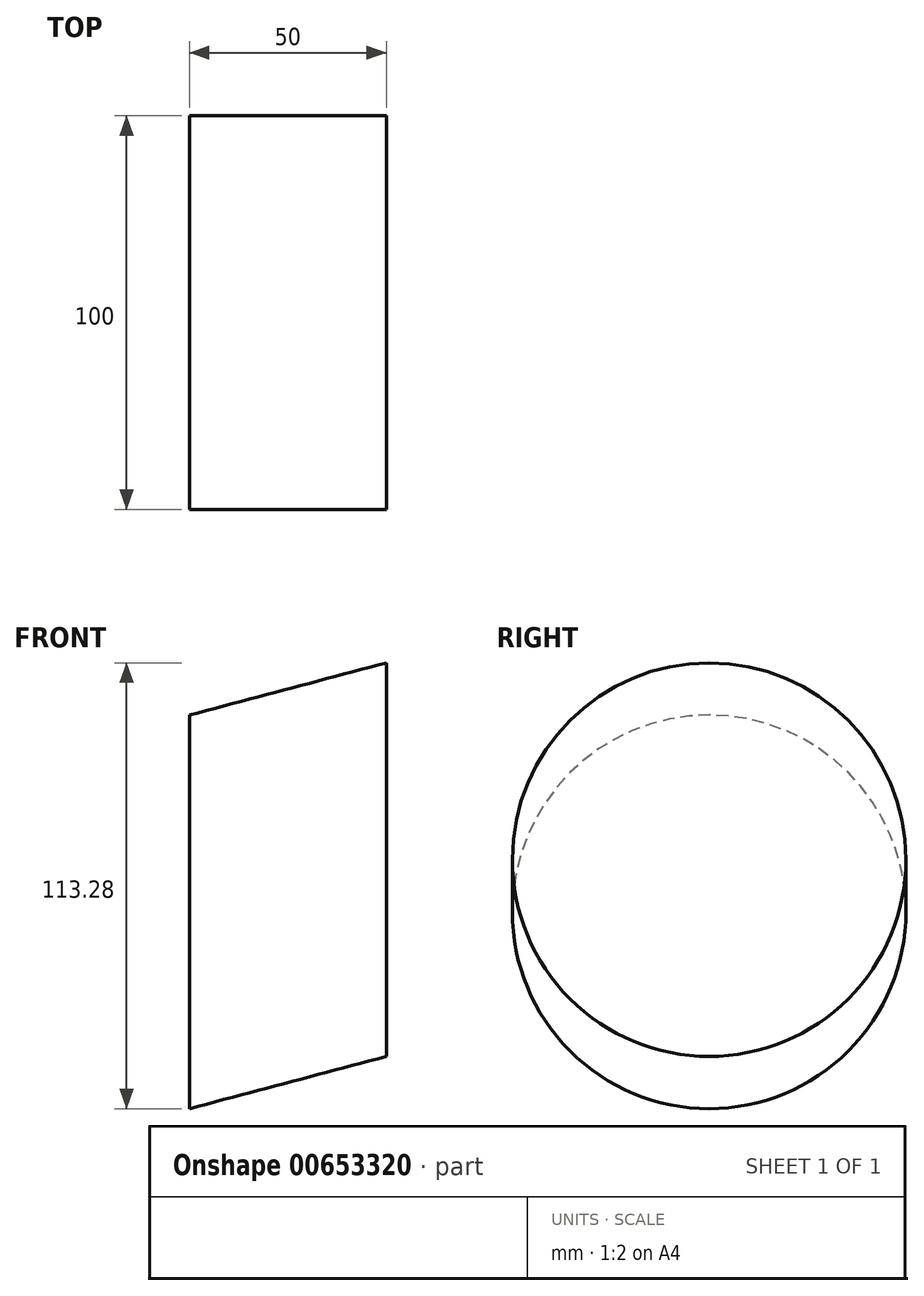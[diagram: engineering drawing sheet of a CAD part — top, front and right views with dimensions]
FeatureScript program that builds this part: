
annotation { "Feature Type Name" : "Feature", "Feature Type Description" : "" }
export const myFeature = defineFeature(function(context is Context, id is Id, definition is map)
    precondition{}
    {
        {
            var Q0;
            Q0=qCreatedBy(makeId("Right.planeOp"),FACE);
            var sketch = newSketch(context, id + "F0", { "sketchPlane" : qUnion([Q0])});
            skCircle(sketch, "E0", {"center": v(0, 0) * mm, "radius": 50 * mm});
            skSolve(sketch);
        }
        {
            var Q0;
            Q0=qCreatedBy(makeId("Right.planeOp"),FACE);
            cPlane(context, id + "F1", {"entities" : qUnion([Q0]), "cplaneType" : CPlaneType.OFFSET, "offset" : 50 * mm, "width" : 150 * mm, "height" : 150 * mm});
        }
        {
            var Q0;
            Q0=qCreatedBy(id+"F1.planeOp",FACE);
            var sketch = newSketch(context, id + "F2", { "sketchPlane" : qUnion([Q0])});
            skCircle(sketch, "E1", {"center": v(0, 13.28) * mm, "radius": 50 * mm});
            skSolve(sketch);
        }
        {
            var Q0;
            Q0=makeQuery(id+"F0.imprint","IMPRINT",FACE,{"disambiguationData":[TD([[makeQuery(id+"F0.imprint","IMPRINT",EDGE,{"derivedFrom":sQuery(id+"F0.wireOp",EDGE,"E0")}),1.0]])]});
            var Q1;
            Q1=makeQuery(id+"F2.imprint","IMPRINT",FACE,{"disambiguationData":[TD([[makeQuery(id+"F2.imprint","IMPRINT",EDGE,{"derivedFrom":sQuery(id+"F2.wireOp",EDGE,"E1")}),1.0]])]});
            loft(context, id + "F3", {"sheetProfilesArray" : [{ "sheetProfileEntities" : qUnion([Q0]) }, { "sheetProfileEntities" : qUnion([Q1]) }]});
        }
    });
